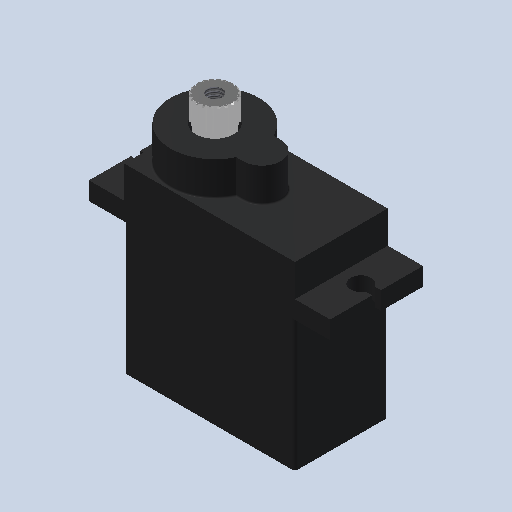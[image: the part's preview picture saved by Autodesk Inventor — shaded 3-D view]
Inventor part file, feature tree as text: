
AUTODESK INVENTOR PART (.ipt)
format: ipt  version: 2023 (Build 270158000, 158)  size: 591,360 bytes
history: native  units: in
note: dims shown in document units (in); Inventor stores cm internally (conversion verified against a paired STEP export)
features: sketch x7, extrude x5, hole x2, fillet x2, mirror x1, pattern_circular x1, chamfer x1, other x1
ambient origin geometry x8: Origin, YZ Plane, XZ Plane, XY Plane, X Axis, Y Axis, Z Axis, Center Point
bodies: Solid1 (feature_tree), Solid2 (feature_tree)
feature tree (20):
  extrude  "Extrusion1"  Depth=0.0945in
  extrude  "Extrusion2"  Depth=0.8976in
  hole  "Hole1"  [1 undecoded]
  extrude  "Extrusion3"  Depth=0.248in
  mirror  "Mirror1"
  fillet  "Fillet1"  Radius=0.2008in
  fillet  "Fillet2"  Radius=0.0376in
  extrude  "Extrusion4"  Depth=0.1693in
  extrude  "Extrusion5"  Depth=0.0974in TaperAngle=0.0deg
  pattern_circular  "Circular Pattern1"  [2 undecoded]
  chamfer  "Chamfer2"  Distance=0.0236in
  hole  "Hole2"  [1 undecoded]
  other  "Ref Sketch"
  sketch  "Sketch1"  dims[d5=0.185in d6=0.0945in]
  sketch  "Sketch2"  dims[d7=0.689in d8=0.8976in]
  sketch  "Sketch3"  dims[d11=0.4882in d12=0.0in d13=0.2323in]
  sketch  "Sketch4"  dims[d14=0.0984in d15=0.248in d16=0.2008in d17=0.0376in]
  sketch  "Sketch5"  dims[d18=0.1772in d19=0.0in d20=0.1693in]
  sketch  "Sketch6"  dims[d21=0.185in]
  sketch  "Sketch7"  dims[d22=0.1083in d23=0.2362in d24=0.1575in d25=0.0787in d26=90.0deg d27=0.315in d28=0.8108in d29=0.1969in d30=0.0in d31=0.0472in d34=0.0236in d35=0.0079in d36=0.0157in d39=0.1719in d41=0.1378in d42=0.3937in d43=0.0in d44=0.0in d50=0.0974in d51=0.0974in d52=0.004in d53=0.0875in d55=0.0124in d56=0.0124in d57=0.0025in d58=0.04in d59=0.0724in d60=0.0272in d61=0.0544in d62=0.04in d63=0.1181in d64=0.0in d65=7.874in d66=360.0deg d68=0.0059in d69=0.0787in d70=45.0deg d71=0.0793in d72=0.2362in d73=0.1575in d74=0.0787in d75=90.0deg d76=0.315in d77=0.8108in d78=0.6654in d79=0.2323in d80=0.2165in d81=1.1024in d86=0.0827in d87=0.8976in d88=0.4882in d89=1.2677in]
note: 4 required parameter values undecoded (feature->parameter linkage not recoverable at this tier; creation-order binding heuristic only, values carry confidence <= 0.55)
